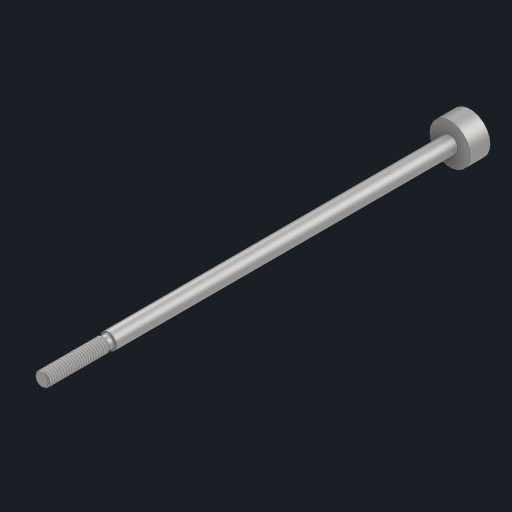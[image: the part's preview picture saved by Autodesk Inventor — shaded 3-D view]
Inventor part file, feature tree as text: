
AUTODESK INVENTOR PART (.ipt)
format: ipt  version: 2023 (Build 270158030, 158C)  size: 121,856 bytes
history: mixed  units: in
note: dims shown in document units (in); Inventor stores cm internally (conversion verified against a paired STEP export)
features: thread x2, imported_body x1
ambient origin geometry x8: Origin, YZ Plane, XZ Plane, XY Plane, X Axis, Y Axis, Z Axis, Center Point
bodies: Solid1 (imported_parasolid)
feature tree (3):
  thread  "Thread1"  [1 undecoded]
  thread  "Threads"  [1 undecoded]
  imported_body  NMx_Import_Brep_tag  [imported B-rep: ~11 faces, bbox_mm=[7.0, 0.0, 105.685]]
note: 2 required parameter values undecoded (feature->parameter linkage not recoverable at this tier; creation-order binding heuristic only, values carry confidence <= 0.55)
